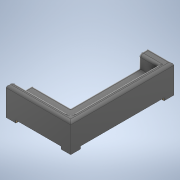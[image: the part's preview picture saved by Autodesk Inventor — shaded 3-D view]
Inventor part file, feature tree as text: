
AUTODESK INVENTOR PART (.ipt)
format: ipt  version: 2022 (Build 260153000, 153)  size: 218,112 bytes
history: native  units: mm
features: extrude x4, sketch x3, fillet x1
ambient origin geometry x8: Origin, YZ Plane, XZ Plane, XY Plane, X Axis, Y Axis, Z Axis, Center Point
bodies: Solid1 (feature_tree)
feature tree (8):
  extrude  "Extrusion1"  Depth=20.0mm
  sketch  "Sketch3"  dims[d2=80.0mm d3=20.0mm]
  extrude  "Extrusion2"  Depth=20.0mm
  extrude  "Extrusion3"  TaperAngle=0.0deg  [1 undecoded]
  fillet  "Fillet1"  Radius=10.0mm
  extrude  "Extrusion4"  Depth=20.0mm
  sketch  "Sketch1"  dims[d0=50.0mm d1=20.0mm]
  sketch  "Sketch4"  dims[d4=0.0mm d5=0.0mm d6=10.0mm d7=0.0mm d8=20.0mm d9=7.5mm d10=5.0mm d11=80.0mm d12=10.0mm d13=0.0mm d14=50.0mm d15=5.0mm d16=10.0mm d17=0.0mm d18=2.0mm d19=7.5mm d20=7.5mm d21=7.5mm d22=7.5mm d23=7.5mm d24=7.5mm d25=7.7mm d26=7.5mm d27=7.5mm d28=7.5mm d29=7.5mm d30=7.5mm d31=2.0mm d32=0.0mm d33=0.0mm d34=0.0mm d35=0.0mm d36=0.0mm]
note: 1 required parameter value undecoded (feature->parameter linkage not recoverable at this tier; creation-order binding heuristic only, values carry confidence <= 0.55)
